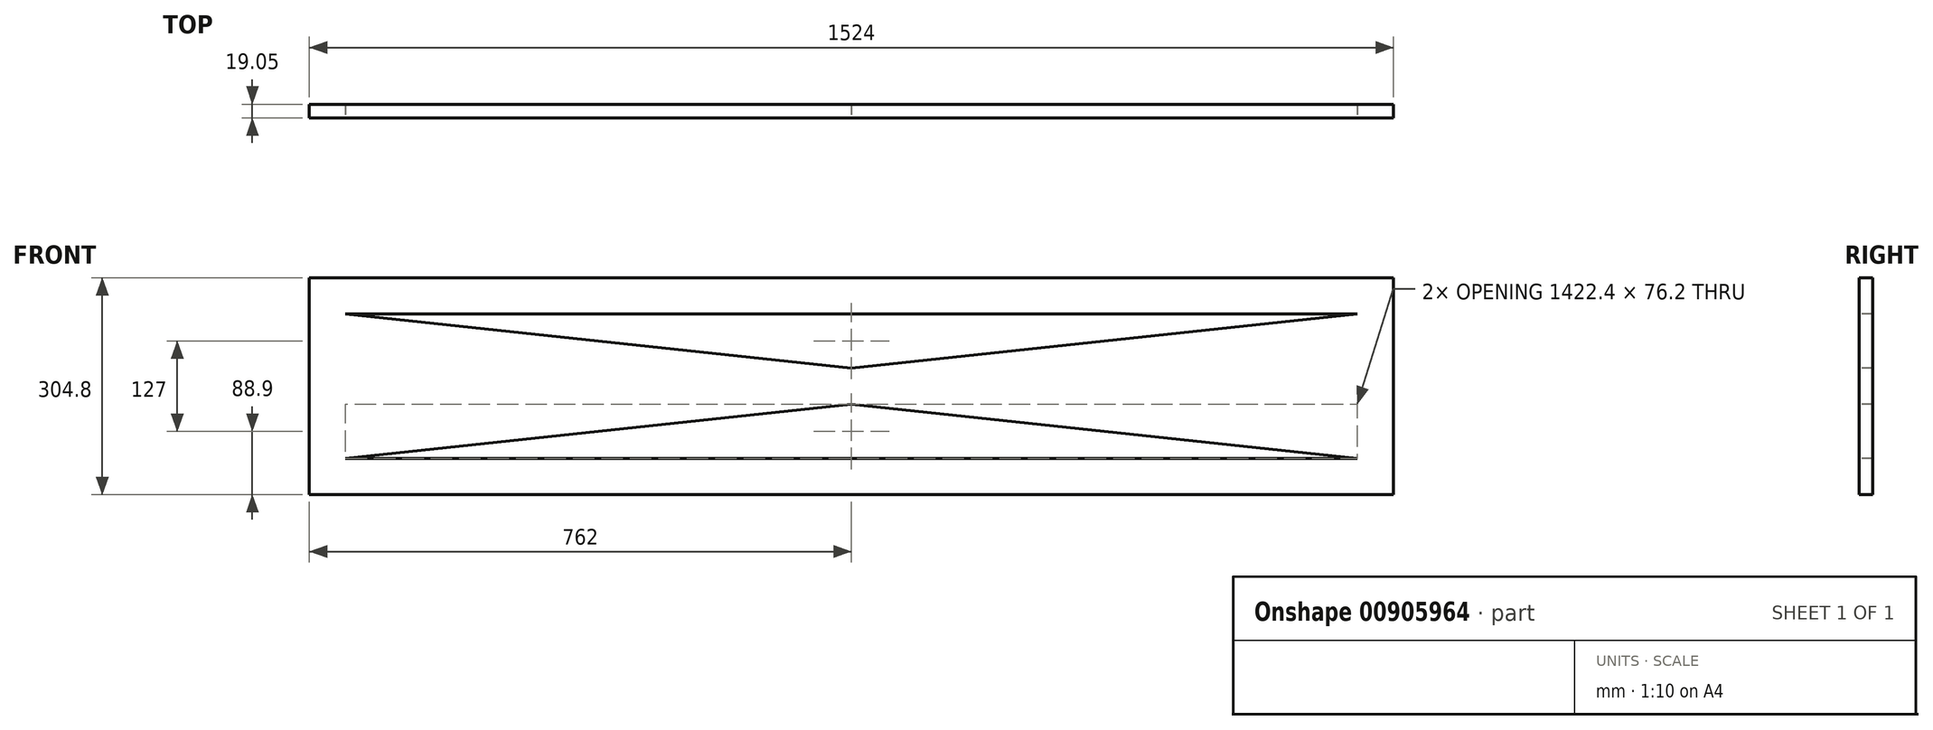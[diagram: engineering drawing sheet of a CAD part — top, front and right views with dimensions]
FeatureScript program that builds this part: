
annotation { "Feature Type Name" : "Feature", "Feature Type Description" : "" }
export const myFeature = defineFeature(function(context is Context, id is Id, definition is map)
    precondition{}
    {
        {
            var Q0;
            Q0=qCreatedBy(makeId("Front.planeOp"),FACE);
            var sketch = newSketch(context, id + "F0", { "sketchPlane" : qUnion([Q0])});
            skLineSegment(sketch, "E0.bottom", {"start": v(0, 0) * mm, "end": v(1524, 0) * mm});
            skLineSegment(sketch, "E0.top", {"start": v(0, 304.8) * mm, "end": v(1524, 304.8) * mm});
            skLineSegment(sketch, "E0.left", {"start": v(0, 0) * mm, "end": v(0, 304.8) * mm});
            skLineSegment(sketch, "E0.right", {"start": v(1524, 0) * mm, "end": v(1524, 304.8) * mm});
            skSolve(sketch);
        }
        {
            var Q0;
            Q0=makeQuery(id+"F0.imprint","IMPRINT",FACE,{"disambiguationData":[TD([[makeQuery(id+"F0.imprint","IMPRINT",EDGE,{"derivedFrom":sQuery(id+"F0.wireOp",EDGE,"E0.bottom")}),1.0]])]});
            extrude(context, id + "F1", {"entities" : qUnion([Q0]), "depth" : 19.05 * mm, "offsetDistance" : 25.4 * mm});
        }
        {
            var Q0;
            Q0=makeQuery(id+"F1.opExtrude","CAP_FACE",FACE,{"disambiguationData":[OSD([sQuery(id+"F0.wireOp",EDGE,"E0.bottom"),sQuery(id+"F0.wireOp",EDGE,"E0.top"),sQuery(id+"F0.wireOp",EDGE,"E0.left"),sQuery(id+"F0.wireOp",EDGE,"E0.right")])],"isStart":false});
            var sketch = newSketch(context, id + "F2", { "sketchPlane" : qUnion([Q0])});
            skLineSegment(sketch, "E1", {"start": v(50.8, 254) * mm, "end": v(1473.2, 254) * mm});
            skLineSegment(sketch, "E2", {"start": v(1473.2, 254) * mm, "end": v(762, 177.8) * mm});
            skLineSegment(sketch, "E3", {"start": v(762, 177.8) * mm, "end": v(50.8, 254) * mm});
            skLineSegment(sketch, "E4", {"start": v(762, 304.8) * mm, "end": v(762, 177.8) * mm, "construction": true});
            skLineSegment(sketch, "E5", {"start": v(0, 152.4) * mm, "end": v(1524, 152.4) * mm, "construction": true});
            skLineSegment(sketch, "E6.MirrorCS", {"start": v(50.8, 50.8) * mm, "end": v(1473.2, 50.8) * mm});
            skLineSegment(sketch, "E7.MirrorCS", {"start": v(1473.2, 50.8) * mm, "end": v(762, 127) * mm});
            skLineSegment(sketch, "E8.MirrorCS", {"start": v(762, 127) * mm, "end": v(50.8, 50.8) * mm});
            skSolve(sketch);
        }
        {
            var Q0;
            Q0 = qSketchRegion(id + "F2", true);
            extrude(context, id + "F3", {"entities" : qUnion([Q0]), "operationType" : NewBodyOperationType.REMOVE, "endBound" : BoundingType.THROUGH_ALL, "oppositeDirection" : true, "depth" : 25.4 * mm, "offsetDistance" : 25.4 * mm});
        }
    });
